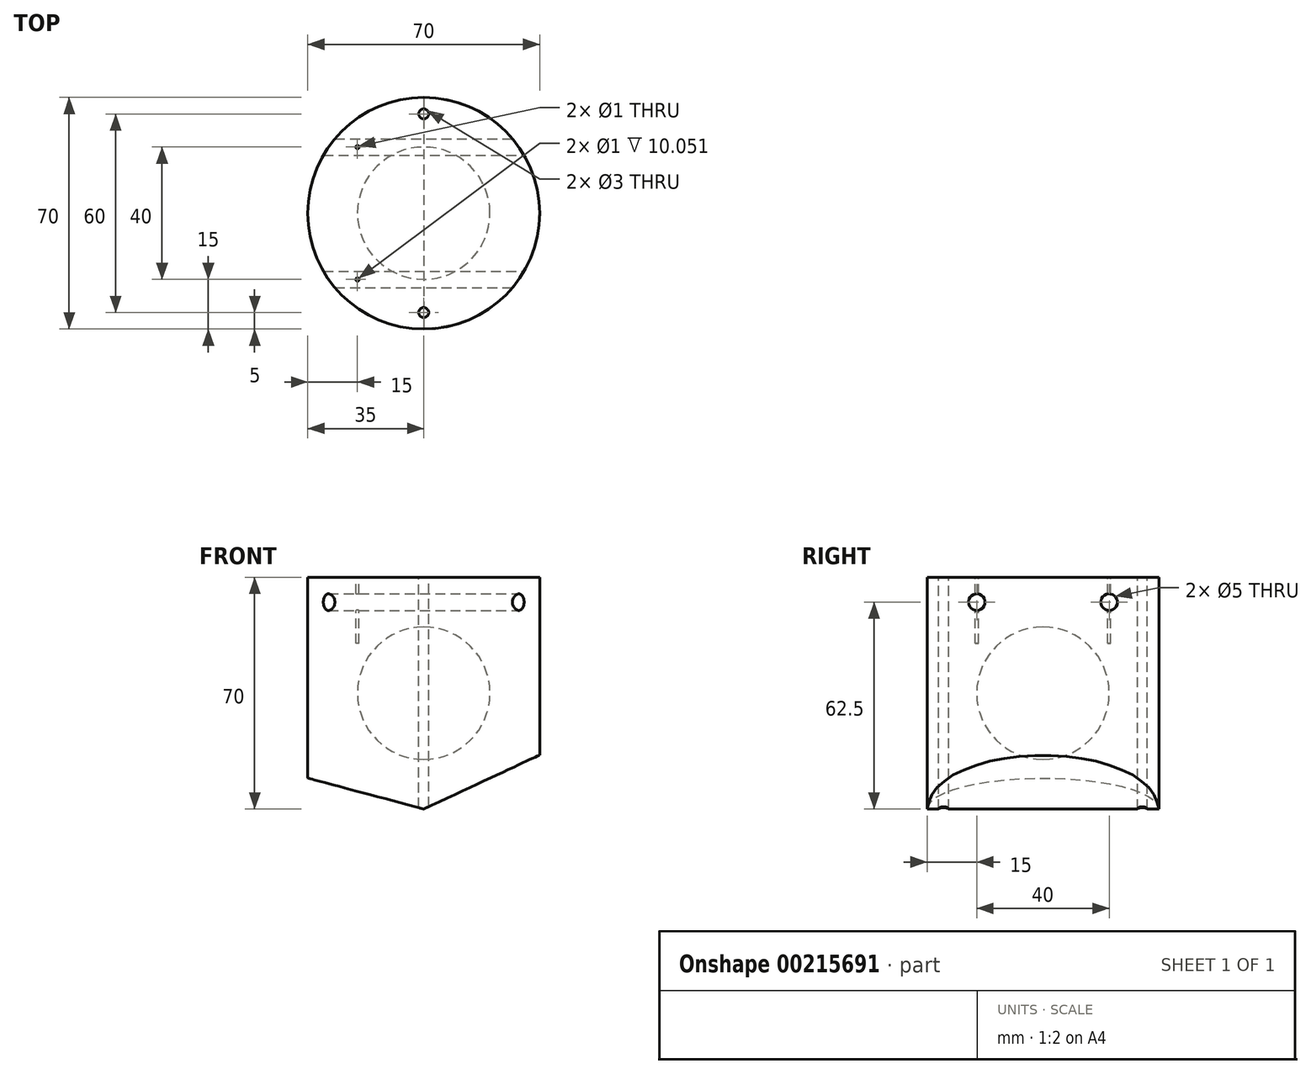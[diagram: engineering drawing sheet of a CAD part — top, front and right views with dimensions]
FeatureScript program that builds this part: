
annotation { "Feature Type Name" : "Feature", "Feature Type Description" : "" }
export const myFeature = defineFeature(function(context is Context, id is Id, definition is map)
    precondition{}
    {
        {
            var Q0;
            Q0=qCreatedBy(makeId("Top.planeOp"),FACE);
            var sketch = newSketch(context, id + "F0", { "sketchPlane" : qUnion([Q0])});
            skCircle(sketch, "E0", {"center": v(0, 0) * mm, "radius": 35 * mm});
            skSolve(sketch);
        }
        {
            var Q0;
            Q0=makeQuery(id+"F0.imprint","IMPRINT",FACE,{"disambiguationData":[TD([[makeQuery(id+"F0.imprint","IMPRINT",EDGE,{"derivedFrom":sQuery(id+"F0.wireOp",EDGE,"E0")}),1.0]])]});
            extrude(context, id + "F1", {"entities" : qUnion([Q0]), "depth" : 70 * mm});
        }
        {
            var Q0;
            Q0=qCreatedBy(makeId("Front.planeOp"),FACE);
            var sketch = newSketch(context, id + "F2", { "sketchPlane" : qUnion([Q0])});
            skLineSegment(sketch, "E1", {"start": v(0, 0) * mm, "end": v(-50, 0) * mm});
            skLineSegment(sketch, "E2", {"start": v(-50, 0) * mm, "end": v(-50, 13.4) * mm});
            skLineSegment(sketch, "E3", {"start": v(-50, 13.4) * mm, "end": v(0, 0) * mm});
            skLineSegment(sketch, "E4", {"start": v(0, 0) * mm, "end": v(50, 23.32) * mm});
            skLineSegment(sketch, "E5", {"start": v(50, 23.32) * mm, "end": v(50, 0) * mm});
            skLineSegment(sketch, "E6", {"start": v(50, 0) * mm, "end": v(0, 0) * mm});
            skSolve(sketch);
        }
        {
            var Q0;
            Q0 = qSketchRegion(id + "F2", true);
            extrude(context, id + "F3", {"entities" : qUnion([Q0]), "operationType" : NewBodyOperationType.REMOVE, "endBound" : BoundingType.THROUGH_ALL, "oppositeDirection" : true, "depth" : 25 * mm, "hasSecondDirection" : true, "secondDirectionBound" : SecondDirectionBoundingType.THROUGH_ALL, "secondDirectionOppositeDirection" : false, "secondDirectionDepth" : 25 * mm});
        }
        {
            var Q0;
            Q0=qCreatedBy(makeId("Right.planeOp"),FACE);
            var sketch = newSketch(context, id + "F4", { "sketchPlane" : qUnion([Q0])});
            skCircle(sketch, "E7", {"center": v(-20, 62.5) * mm, "radius": 2.5 * mm});
            skCircle(sketch, "E8.MirrorC", {"center": v(20, 62.5) * mm, "radius": 2.5 * mm});
            skSolve(sketch);
        }
        {
            var Q0;
            Q0 = qSketchRegion(id + "F4", true);
            extrude(context, id + "F5", {"entities" : qUnion([Q0]), "operationType" : NewBodyOperationType.REMOVE, "endBound" : BoundingType.THROUGH_ALL, "oppositeDirection" : true, "depth" : 25 * mm, "hasSecondDirection" : true, "secondDirectionBound" : SecondDirectionBoundingType.THROUGH_ALL, "secondDirectionOppositeDirection" : false, "secondDirectionDepth" : 25 * mm});
        }
        {
            var Q0;
            Q0=qCreatedBy(makeId("Front.planeOp"),FACE);
            var sketch = newSketch(context, id + "F6", { "sketchPlane" : qUnion([Q0])});
            skArc(sketch, "E9", {"start": v(0, 55) * mm, "mid": v(-20, 35) * mm, "end": v(0, 15) * mm});
            skLineSegment(sketch, "E10", {"start": v(0, 55) * mm, "end": v(0, 15) * mm});
            skSolve(sketch);
        }
        {
            var Q0;
            Q0 = qSketchRegion(id + "F6", true);
            var Q1;
            Q1=sQuery(id+"F6.wireOp",EDGE,"E9");
            var Q2;
            Q2=sQuery(id+"F6.wireOp",EDGE,"E10");
            revolve(context, id + "F7", {"operationType" : NewBodyOperationType.REMOVE, "entities" : qUnion([Q0]), "surfaceEntities" : qUnion([Q1]), "axis" : qUnion([Q2]), "revolveType" : RevolveType.ONE_DIRECTION, "angle" : 360 * degree});
        }
        {
            var Q0;
            Q0=makeQuery(id+"F1.opExtrude","CAP_FACE",FACE,{"disambiguationData":[OSD([sQuery(id+"F0.wireOp",EDGE,"E0")])],"isStart":false});
            var sketch = newSketch(context, id + "F8", { "sketchPlane" : qUnion([Q0])});
            skCircle(sketch, "E11", {"center": v(-20, 20) * mm, "radius": 0.5 * mm});
            skCircle(sketch, "E12.MirrorC", {"center": v(-20, -20) * mm, "radius": 0.5 * mm});
            skSolve(sketch);
        }
        {
            var Q0;
            Q0 = qSketchRegion(id + "F8", true);
            extrude(context, id + "F9", {"entities" : qUnion([Q0]), "operationType" : NewBodyOperationType.REMOVE, "oppositeDirection" : true, "depth" : 20 * mm});
        }
        {
            var Q0;
            Q0=makeQuery(id+"F1.opExtrude","CAP_FACE",FACE,{"disambiguationData":[OSD([sQuery(id+"F0.wireOp",EDGE,"E0")])],"isStart":false});
            var sketch = newSketch(context, id + "F10", { "sketchPlane" : qUnion([Q0])});
            skCircle(sketch, "E13", {"center": v(0, 30) * mm, "radius": 1.5 * mm});
            skCircle(sketch, "E14.MirrorC", {"center": v(0, -30) * mm, "radius": 1.5 * mm});
            skSolve(sketch);
        }
        {
            var Q0;
            Q0 = qSketchRegion(id + "F10", true);
            extrude(context, id + "F11", {"entities" : qUnion([Q0]), "operationType" : NewBodyOperationType.REMOVE, "endBound" : BoundingType.THROUGH_ALL, "oppositeDirection" : true, "depth" : 25 * mm});
        }
    });
